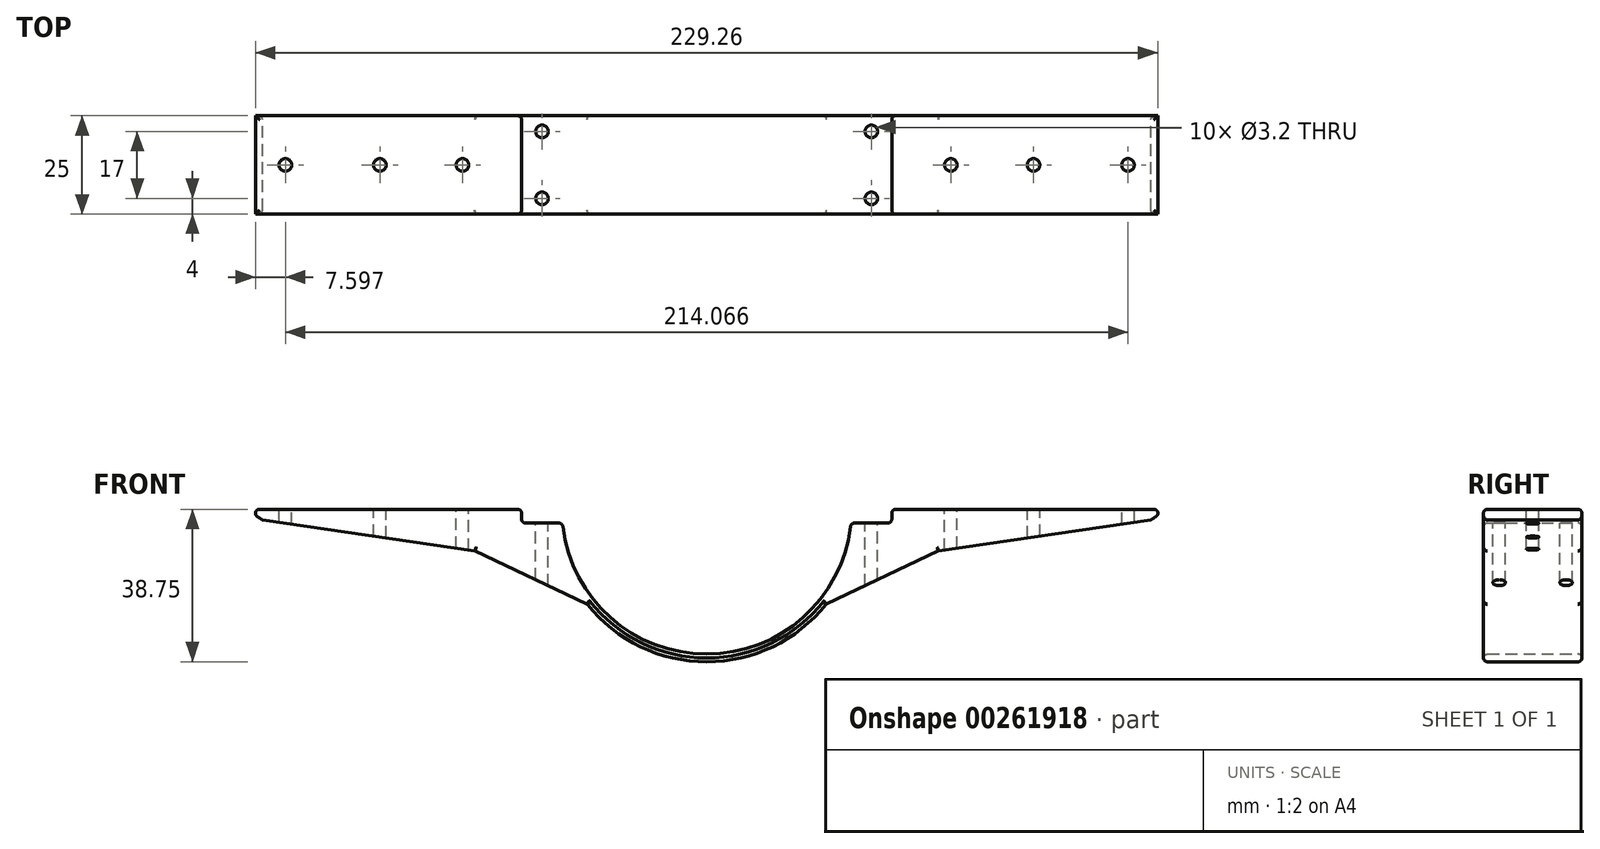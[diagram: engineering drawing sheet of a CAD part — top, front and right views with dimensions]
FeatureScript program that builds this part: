
annotation { "Feature Type Name" : "Feature", "Feature Type Description" : "" }
export const myFeature = defineFeature(function(context is Context, id is Id, definition is map)
    precondition{}
    {
        {
            var Q0;
            Q0=qCreatedBy(makeId("Front.planeOp"),FACE);
            var sketch = newSketch(context, id + "F0", { "sketchPlane" : qUnion([Q0])});
            skLineSegment(sketch, "E0", {"start": v(36.63, -3.5) * mm, "end": v(47.03, -3.5) * mm});
            skLineSegment(sketch, "E1", {"start": v(47.03, -3.5) * mm, "end": v(47.03, 0) * mm});
            skLineSegment(sketch, "E2", {"start": v(47.03, 0) * mm, "end": v(117.03, 0) * mm});
            skLineSegment(sketch, "E3", {"start": v(117.03, 0) * mm, "end": v(112.83, -2.7) * mm});
            skLineSegment(sketch, "E4", {"start": v(112.83, -2.7) * mm, "end": v(58.86, -10.59) * mm});
            skLineSegment(sketch, "E5", {"start": v(58.86, -10.59) * mm, "end": v(30.37, -24.06) * mm});
            skLineSegment(sketch, "E6.MirrorCS", {"start": v(-47.03, 0) * mm, "end": v(-117.03, 0) * mm});
            skLineSegment(sketch, "E7.MirrorCS", {"start": v(-117.03, 0) * mm, "end": v(-112.83, -2.7) * mm});
            skLineSegment(sketch, "E8.MirrorCS", {"start": v(-112.83, -2.7) * mm, "end": v(-58.86, -10.59) * mm});
            skLineSegment(sketch, "E9.MirrorCS", {"start": v(-58.86, -10.59) * mm, "end": v(-30.37, -24.06) * mm});
            skLineSegment(sketch, "E10.MirrorCS", {"start": v(-47.03, -3.5) * mm, "end": v(-47.03, 0) * mm});
            skArc(sketch, "E11", {"start": v(-30.37, -24.06) * mm, "mid": v(0, -38.75) * mm, "end": v(30.37, -24.06) * mm});
            skArc(sketch, "E12", {"start": v(-36.63, -3.5) * mm, "mid": v(0, -36.8) * mm, "end": v(36.63, -3.5) * mm});
            skLineSegment(sketch, "E13.MirrorCS", {"start": v(-36.63, -3.5) * mm, "end": v(-47.03, -3.5) * mm});
            skCircle(sketch, "E14", {"center": v(0, 0) * mm, "radius": 36.8 * mm, "construction": true});
            skSolve(sketch);
        }
        {
            var Q0;
            Q0 = qSketchRegion(id + "F0", true);
            extrude(context, id + "F1", {"entities" : qUnion([Q0]), "depth" : 25 * mm});
        }
        {
            var Q0;
            Q0=makeQuery(id+"F1.opExtrude","SWEPT_FACE",FACE,{"disambiguationData":[OSD([sQuery(id+"F0.wireOp",EDGE,"E0")])]});
            var sketch = newSketch(context, id + "F2", { "sketchPlane" : qUnion([Q0])});
            skLineSegment(sketch, "E15.0", {"start": v(36.63, -25) * mm, "end": v(36.63, 0) * mm, "construction": true});
            skLineSegment(sketch, "E16.0", {"start": v(47.03, -25) * mm, "end": v(47.03, 0) * mm, "construction": true});
            skLineSegment(sketch, "E17.0", {"start": v(36.63, 0) * mm, "end": v(47.03, 0) * mm, "construction": true});
            skLineSegment(sketch, "E18.0", {"start": v(36.63, -25) * mm, "end": v(47.03, -25) * mm, "construction": true});
            skCircle(sketch, "E19", {"center": v(41.83, -4) * mm, "radius": 1.5 * mm, "construction": true});
            skCircle(sketch, "E20", {"center": v(41.83, -21) * mm, "radius": 1.5 * mm, "construction": true});
            skLineSegment(sketch, "E21", {"start": v(41.83, 3.44) * mm, "end": v(41.83, -28) * mm, "construction": true});
            skPoint(sketch, "E21.startSnap0", {"position": v(41.83, 0) * mm});
            skLineSegment(sketch, "E22.0", {"start": v(47.03, 0) * mm, "end": v(117.03, 0) * mm, "construction": true});
            skLineSegment(sketch, "E23.0", {"start": v(117.03, -25) * mm, "end": v(117.03, 0) * mm, "construction": true});
            skLineSegment(sketch, "E24.0", {"start": v(47.03, -25) * mm, "end": v(117.03, -25) * mm, "construction": true});
            skCircle(sketch, "E25.MirrorC", {"center": v(-41.83, -4) * mm, "radius": 1.5 * mm, "construction": true});
            skCircle(sketch, "E26.MirrorC", {"center": v(-41.83, -21) * mm, "radius": 1.5 * mm, "construction": true});
            skSolve(sketch);
        }
        {
            var Q0;
            Q0=sQuery(id+"F2.wireOp",VERTEX,"E25.MirrorC.center");
            var Q1;
            Q1=sQuery(id+"F2.wireOp",VERTEX,"E26.MirrorC.center");
            var Q2;
            Q2=sQuery(id+"F2.wireOp",VERTEX,"E19.center");
            var Q3;
            Q3=sQuery(id+"F2.wireOp",VERTEX,"E20.center");
            var Q4;
            Q4=sQuery(id+"F2.wireOp",VERTEX,"532dbcc8-0f18-4713-bc69-76903608bbd60.MirrorC.center");
            var Q5;
            Q5=sQuery(id+"F2.wireOp",VERTEX,"9e031427-b27b-4900-8835-da2c1723c3770.MirrorC.center");
            var Q6;
            Q6=sQuery(id+"F2.wireOp",VERTEX,"4787d6b4-0633-4151-8f98-541dbca428990.MirrorC.center");
            var Q7;
            Q7=sQuery(id+"F2.wireOp",VERTEX,"2Y8P0mAt-mXRv-PHkJ-mauT-ijigYykqqnIH.center");
            var Q8;
            Q8=sQuery(id+"F2.wireOp",VERTEX,"llFoWV4t-3RB5-LzZy-609j-9WCmL490HZSf.center");
            var Q9;
            Q9=sQuery(id+"F2.wireOp",VERTEX,"XDAml7uU-22in-n0Eo-OKlj-WeZyBotYBq0C.center");
            var Q10;
            Q10=makeQuery(id+"F1.opExtrude","SWEPT_BODY",BODY,{"disambiguationData":[OSD([sQuery(id+"F0.wireOp",EDGE,"E0"),sQuery(id+"F0.wireOp",EDGE,"E1"),sQuery(id+"F0.wireOp",EDGE,"E2"),sQuery(id+"F0.wireOp",EDGE,"E3"),sQuery(id+"F0.wireOp",EDGE,"E4"),sQuery(id+"F0.wireOp",EDGE,"E5"),sQuery(id+"F0.wireOp",EDGE,"E6.MirrorCS"),sQuery(id+"F0.wireOp",EDGE,"E7.MirrorCS"),sQuery(id+"F0.wireOp",EDGE,"E8.MirrorCS"),sQuery(id+"F0.wireOp",EDGE,"E9.MirrorCS"),sQuery(id+"F0.wireOp",EDGE,"E10.MirrorCS"),sQuery(id+"F0.wireOp",EDGE,"E11"),sQuery(id+"F0.wireOp",EDGE,"E12"),sQuery(id+"F0.wireOp",EDGE,"E13.MirrorCS")])]});
            hole(context, id + "F3", {"style" : HoleStyle.SIMPLE, "endStyle" : HoleEndStyle.THROUGH, "standardTappedOrClearance" : lookupTablePath({ "standard" : "ISO", "engagement" : "75%", "pitch" : "0.75 mm", "size" : "M4", "type" : "Tapped" }), "standardBlindInLast" : lookupTablePath({ "standard" : "ISO", "engagement" : "75%", "pitch" : "0.75 mm", "size" : "M4", "type" : "Tapped" }), "holeDiameter" : 3.2 * mm, "showTappedDepth" : true, "tappedDepth" : 12 * mm, "tapClearance" : 3, "locations" : qUnion([Q0, Q1, Q2, Q3, Q4, Q5, Q6, Q7, Q8, Q9]), "scope" : qUnion([Q10])});
        }
        {
            var Q0;
            Q0=makeQuery(id+"F1.opExtrude","SWEPT_FACE",FACE,{"disambiguationData":[OSD([sQuery(id+"F0.wireOp",EDGE,"E2")])]});
            var sketch = newSketch(context, id + "F4", { "sketchPlane" : qUnion([Q0])});
            skLineSegment(sketch, "E27.0", {"start": v(47.03, -25) * mm, "end": v(47.03, 0) * mm, "construction": true});
            skLineSegment(sketch, "E28.0", {"start": v(47.03, 0) * mm, "end": v(117.03, 0) * mm, "construction": true});
            skLineSegment(sketch, "E29.0", {"start": v(117.03, -25) * mm, "end": v(117.03, 0) * mm, "construction": true});
            skLineSegment(sketch, "E30.0", {"start": v(47.03, -25) * mm, "end": v(117.03, -25) * mm, "construction": true});
            skLineSegment(sketch, "E31", {"start": v(-4.17, -12.5) * mm, "end": v(128.24, -12.5) * mm, "construction": true});
            skCircle(sketch, "E32", {"center": v(62.03, -12.5) * mm, "radius": 1.5 * mm, "construction": true});
            skCircle(sketch, "E33", {"center": v(83.03, -12.5) * mm, "radius": 1.5 * mm, "construction": true});
            skCircle(sketch, "E34", {"center": v(107.03, -12.5) * mm, "radius": 1.5 * mm, "construction": true});
            skCircle(sketch, "E35.MirrorC", {"center": v(-62.03, -12.5) * mm, "radius": 1.5 * mm, "construction": true});
            skCircle(sketch, "E36.MirrorC", {"center": v(-107.03, -12.5) * mm, "radius": 1.5 * mm, "construction": true});
            skLineSegment(sketch, "E37.MirrorCS", {"start": v(4.17, -12.5) * mm, "end": v(-128.24, -12.5) * mm, "construction": true});
            skCircle(sketch, "E38.MirrorC", {"center": v(-83.03, -12.5) * mm, "radius": 1.5 * mm, "construction": true});
            skSolve(sketch);
        }
        {
            var Q0;
            Q0=sQuery(id+"F4.wireOp",VERTEX,"E36.MirrorC.center");
            var Q1;
            Q1=sQuery(id+"F4.wireOp",VERTEX,"E38.MirrorC.center");
            var Q2;
            Q2=sQuery(id+"F4.wireOp",VERTEX,"E35.MirrorC.center");
            var Q3;
            Q3=sQuery(id+"F4.wireOp",VERTEX,"E32.center");
            var Q4;
            Q4=sQuery(id+"F4.wireOp",VERTEX,"E33.center");
            var Q5;
            Q5=sQuery(id+"F4.wireOp",VERTEX,"E34.center");
            var Q6;
            Q6=makeQuery(id+"F1.opExtrude","SWEPT_BODY",BODY,{"disambiguationData":[OSD([sQuery(id+"F0.wireOp",EDGE,"E0"),sQuery(id+"F0.wireOp",EDGE,"E1"),sQuery(id+"F0.wireOp",EDGE,"E2"),sQuery(id+"F0.wireOp",EDGE,"E3"),sQuery(id+"F0.wireOp",EDGE,"E4"),sQuery(id+"F0.wireOp",EDGE,"E5"),sQuery(id+"F0.wireOp",EDGE,"E6.MirrorCS"),sQuery(id+"F0.wireOp",EDGE,"E7.MirrorCS"),sQuery(id+"F0.wireOp",EDGE,"E8.MirrorCS"),sQuery(id+"F0.wireOp",EDGE,"E9.MirrorCS"),sQuery(id+"F0.wireOp",EDGE,"E10.MirrorCS"),sQuery(id+"F0.wireOp",EDGE,"E11"),sQuery(id+"F0.wireOp",EDGE,"E12"),sQuery(id+"F0.wireOp",EDGE,"E13.MirrorCS")])]});
            hole(context, id + "F5", {"style" : HoleStyle.SIMPLE, "endStyle" : HoleEndStyle.THROUGH, "standardTappedOrClearance" : lookupTablePath({ "standard" : "ISO", "engagement" : "75%", "pitch" : "0.75 mm", "size" : "M4", "type" : "Tapped" }), "standardBlindInLast" : lookupTablePath({ "standard" : "ISO", "engagement" : "75%", "pitch" : "0.75 mm", "size" : "M4", "type" : "Tapped" }), "holeDiameter" : 3.2 * mm, "showTappedDepth" : true, "tappedDepth" : 12 * mm, "tapClearance" : 3, "locations" : qUnion([Q0, Q1, Q2, Q3, Q4, Q5]), "scope" : qUnion([Q6])});
        }
        {
            var Q0;
            Q0=makeQuery(id+"F1.opExtrude","CAP_EDGE",EDGE,{"disambiguationData":[OSD([sQuery(id+"F0.wireOp",EDGE,"E2")])],"isStart":true});
            var Q1;
            Q1=makeQuery(id+"F1.opExtrude","CAP_EDGE",EDGE,{"disambiguationData":[OSD([sQuery(id+"F0.wireOp",EDGE,"E2")])],"isStart":false});
            var Q2;
            Q2=makeQuery(id+"F1.opExtrude","SWEPT_EDGE",EDGE,{"disambiguationData":[OSD([sQuery(id+"F0.wireOp",EDGE,"E2"),sQuery(id+"F0.wireOp",EDGE,"E3")])]});
            var Q3;
            Q3=makeQuery(id+"F1.opExtrude","SWEPT_EDGE",EDGE,{"disambiguationData":[OSD([sQuery(id+"F0.wireOp",EDGE,"E1"),sQuery(id+"F0.wireOp",EDGE,"E2")])]});
            var Q4;
            Q4=makeQuery(id+"F1.opExtrude","SWEPT_EDGE",EDGE,{"disambiguationData":[OSD([sQuery(id+"F0.wireOp",EDGE,"E0"),sQuery(id+"F0.wireOp",EDGE,"E12")])]});
            var Q5;
            Q5=makeQuery(id+"F1.opExtrude","CAP_EDGE",EDGE,{"disambiguationData":[OSD([sQuery(id+"F0.wireOp",EDGE,"E12")])],"isStart":true});
            var Q6;
            Q6=makeQuery(id+"F1.opExtrude","CAP_EDGE",EDGE,{"disambiguationData":[OSD([sQuery(id+"F0.wireOp",EDGE,"E12")])],"isStart":false});
            var Q7;
            Q7=makeQuery(id+"F1.opExtrude","CAP_EDGE",EDGE,{"disambiguationData":[OSD([sQuery(id+"F0.wireOp",EDGE,"E0")])],"isStart":true});
            var Q8;
            Q8=makeQuery(id+"F1.opExtrude","CAP_EDGE",EDGE,{"disambiguationData":[OSD([sQuery(id+"F0.wireOp",EDGE,"E1")])],"isStart":true});
            var Q9;
            Q9=makeQuery(id+"F1.opExtrude","SWEPT_EDGE",EDGE,{"disambiguationData":[OSD([sQuery(id+"F0.wireOp",EDGE,"E0"),sQuery(id+"F0.wireOp",EDGE,"E1")])]});
            var Q10;
            Q10=makeQuery(id+"F1.opExtrude","CAP_EDGE",EDGE,{"disambiguationData":[OSD([sQuery(id+"F0.wireOp",EDGE,"E1")])],"isStart":false});
            var Q11;
            Q11=makeQuery(id+"F1.opExtrude","CAP_EDGE",EDGE,{"disambiguationData":[OSD([sQuery(id+"F0.wireOp",EDGE,"E0")])],"isStart":false});
            var Q12;
            Q12=makeQuery(id+"F1.opExtrude","SWEPT_EDGE",EDGE,{"disambiguationData":[OSD([sQuery(id+"F0.wireOp",EDGE,"E12"),sQuery(id+"F0.wireOp",EDGE,"E13.MirrorCS")])]});
            var Q13;
            Q13=makeQuery(id+"F1.opExtrude","CAP_EDGE",EDGE,{"disambiguationData":[OSD([sQuery(id+"F0.wireOp",EDGE,"E13.MirrorCS")])],"isStart":true});
            var Q14;
            Q14=makeQuery(id+"F1.opExtrude","CAP_EDGE",EDGE,{"disambiguationData":[OSD([sQuery(id+"F0.wireOp",EDGE,"E10.MirrorCS")])],"isStart":true});
            var Q15;
            Q15=makeQuery(id+"F1.opExtrude","SWEPT_EDGE",EDGE,{"disambiguationData":[OSD([sQuery(id+"F0.wireOp",EDGE,"E6.MirrorCS"),sQuery(id+"F0.wireOp",EDGE,"E10.MirrorCS")])]});
            var Q16;
            Q16=makeQuery(id+"F1.opExtrude","CAP_EDGE",EDGE,{"disambiguationData":[OSD([sQuery(id+"F0.wireOp",EDGE,"E13.MirrorCS")])],"isStart":false});
            var Q17;
            Q17=makeQuery(id+"F1.opExtrude","CAP_EDGE",EDGE,{"disambiguationData":[OSD([sQuery(id+"F0.wireOp",EDGE,"E6.MirrorCS")])],"isStart":true});
            var Q18;
            Q18=makeQuery(id+"F1.opExtrude","CAP_EDGE",EDGE,{"disambiguationData":[OSD([sQuery(id+"F0.wireOp",EDGE,"E10.MirrorCS")])],"isStart":false});
            var Q19;
            Q19=makeQuery(id+"F1.opExtrude","SWEPT_EDGE",EDGE,{"disambiguationData":[OSD([sQuery(id+"F0.wireOp",EDGE,"E10.MirrorCS"),sQuery(id+"F0.wireOp",EDGE,"E13.MirrorCS")])]});
            var Q20;
            Q20=makeQuery(id+"F1.opExtrude","CAP_EDGE",EDGE,{"disambiguationData":[OSD([sQuery(id+"F0.wireOp",EDGE,"E6.MirrorCS")])],"isStart":false});
            var Q21;
            Q21=makeQuery(id+"F1.opExtrude","SWEPT_EDGE",EDGE,{"disambiguationData":[OSD([sQuery(id+"F0.wireOp",EDGE,"E6.MirrorCS"),sQuery(id+"F0.wireOp",EDGE,"E7.MirrorCS")])]});
            fillet(context, id + "F6", {"entities" : qUnion([Q0, Q1, Q2, Q3, Q4, Q5, Q6, Q7, Q8, Q9, Q10, Q11, Q12, Q13, Q14, Q15, Q16, Q17, Q18, Q19, Q20, Q21]), "radius" : 1 * mm, "tangentPropagation" : true, "allowEdgeOverflow" : false});
        }
        {
            var Q0;
            Q0=makeQuery(id+"F1.opExtrude","CAP_EDGE",EDGE,{"disambiguationData":[OSD([sQuery(id+"F0.wireOp",EDGE,"E9.MirrorCS")])],"isStart":true});
            var Q1;
            Q1=makeQuery(id+"F1.opExtrude","CAP_EDGE",EDGE,{"disambiguationData":[OSD([sQuery(id+"F0.wireOp",EDGE,"E8.MirrorCS")])],"isStart":false});
            var Q2;
            Q2=makeQuery(id+"F1.opExtrude","CAP_EDGE",EDGE,{"disambiguationData":[OSD([sQuery(id+"F0.wireOp",EDGE,"E9.MirrorCS")])],"isStart":false});
            var Q3;
            Q3=makeQuery(id+"F1.opExtrude","CAP_EDGE",EDGE,{"disambiguationData":[OSD([sQuery(id+"F0.wireOp",EDGE,"E11")])],"isStart":false});
            var Q4;
            Q4=makeQuery(id+"F1.opExtrude","CAP_EDGE",EDGE,{"disambiguationData":[OSD([sQuery(id+"F0.wireOp",EDGE,"E11")])],"isStart":true});
            var Q5;
            Q5=makeQuery(id+"F1.opExtrude","CAP_EDGE",EDGE,{"disambiguationData":[OSD([sQuery(id+"F0.wireOp",EDGE,"E8.MirrorCS")])],"isStart":true});
            var Q6;
            Q6=makeQuery(id+"F1.opExtrude","CAP_EDGE",EDGE,{"disambiguationData":[OSD([sQuery(id+"F0.wireOp",EDGE,"E4")])],"isStart":false});
            var Q7;
            Q7=makeQuery(id+"F1.opExtrude","CAP_EDGE",EDGE,{"disambiguationData":[OSD([sQuery(id+"F0.wireOp",EDGE,"E5")])],"isStart":true});
            var Q8;
            Q8=makeQuery(id+"F1.opExtrude","CAP_EDGE",EDGE,{"disambiguationData":[OSD([sQuery(id+"F0.wireOp",EDGE,"E4")])],"isStart":true});
            var Q9;
            Q9=makeQuery(id+"F1.opExtrude","CAP_EDGE",EDGE,{"disambiguationData":[OSD([sQuery(id+"F0.wireOp",EDGE,"E5")])],"isStart":false});
            fillet(context, id + "F7", {"entities" : qUnion([Q0, Q1, Q2, Q3, Q4, Q5, Q6, Q7, Q8, Q9]), "radius" : 1 * mm, "tangentPropagation" : true, "allowEdgeOverflow" : false});
        }
        {
            var Q0;
            Q0=makeQuery(id+"F1.opExtrude","SWEPT_EDGE",EDGE,{"disambiguationData":[OSD([sQuery(id+"F0.wireOp",EDGE,"E5"),sQuery(id+"F0.wireOp",EDGE,"E11")])]});
            var Q1;
            Q1=makeQuery(id+"F1.opExtrude","SWEPT_EDGE",EDGE,{"disambiguationData":[OSD([sQuery(id+"F0.wireOp",EDGE,"E4"),sQuery(id+"F0.wireOp",EDGE,"E5")])]});
            var Q2;
            Q2=makeQuery(id+"F1.opExtrude","SWEPT_EDGE",EDGE,{"disambiguationData":[OSD([sQuery(id+"F0.wireOp",EDGE,"E9.MirrorCS"),sQuery(id+"F0.wireOp",EDGE,"E11")])]});
            var Q3;
            Q3=makeQuery(id+"F1.opExtrude","SWEPT_EDGE",EDGE,{"disambiguationData":[OSD([sQuery(id+"F0.wireOp",EDGE,"E8.MirrorCS"),sQuery(id+"F0.wireOp",EDGE,"E9.MirrorCS")])]});
            fillet(context, id + "F8", {"entities" : qUnion([Q0, Q1, Q2, Q3]), "radius" : .5 * mm, "tangentPropagation" : true, "allowEdgeOverflow" : false});
        }
    });
